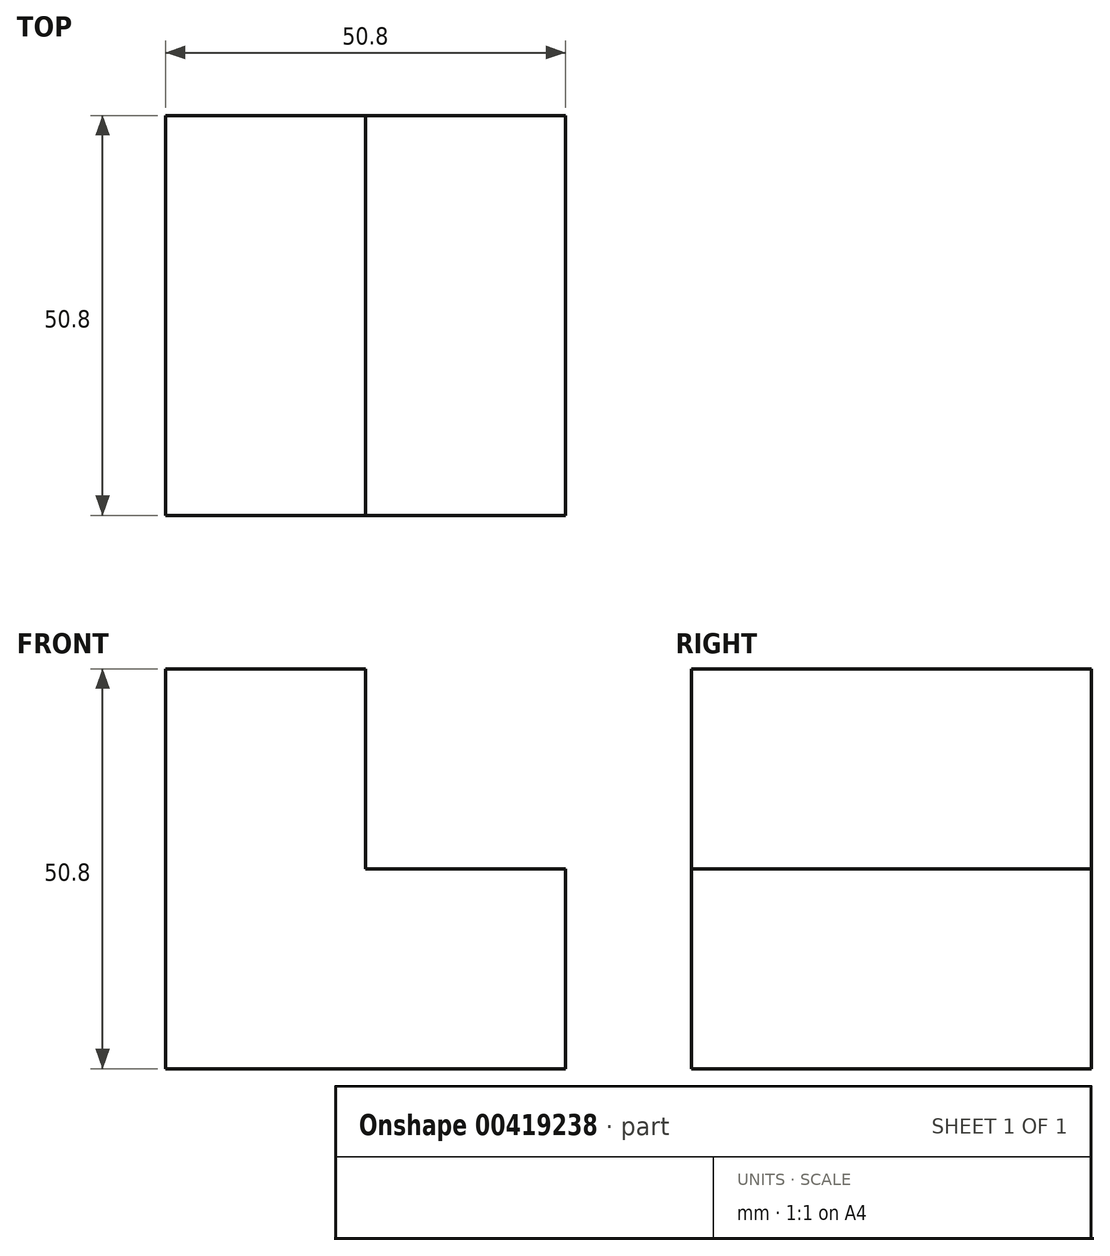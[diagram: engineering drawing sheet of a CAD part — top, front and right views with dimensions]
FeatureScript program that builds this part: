
annotation { "Feature Type Name" : "Feature", "Feature Type Description" : "" }
export const myFeature = defineFeature(function(context is Context, id is Id, definition is map)
    precondition{}
    {
        {
            var Q0;
            Q0=qCreatedBy(makeId("Front.planeOp"),FACE);
            var sketch = newSketch(context, id + "F0", { "sketchPlane" : qUnion([Q0])});
            skLineSegment(sketch, "E0", {"start": v(0, 0) * mm, "end": v(-25.4, 0) * mm});
            skLineSegment(sketch, "E1", {"start": v(-25.4, 25.4) * mm, "end": v(-25.4, 0) * mm});
            skLineSegment(sketch, "E2", {"start": v(-25.4, 25.4) * mm, "end": v(-25.4, 50.8) * mm});
            skLineSegment(sketch, "E3", {"start": v(0, 50.8) * mm, "end": v(-25.4, 50.8) * mm});
            skLineSegment(sketch, "E4", {"start": v(0, 50.8) * mm, "end": v(0, 25.4) * mm});
            skLineSegment(sketch, "E5", {"start": v(0, 25.4) * mm, "end": v(25.4, 25.4) * mm});
            skLineSegment(sketch, "E6", {"start": v(25.4, 25.4) * mm, "end": v(25.4, 0) * mm});
            skLineSegment(sketch, "E7", {"start": v(25.4, 0) * mm, "end": v(0, 0) * mm});
            skSolve(sketch);
        }
        {
            var Q0;
            Q0 = qSketchRegion(id + "F0", true);
            extrude(context, id + "F1", {"entities" : qUnion([Q0]), "depth" : 50.8 * mm});
        }
    });
